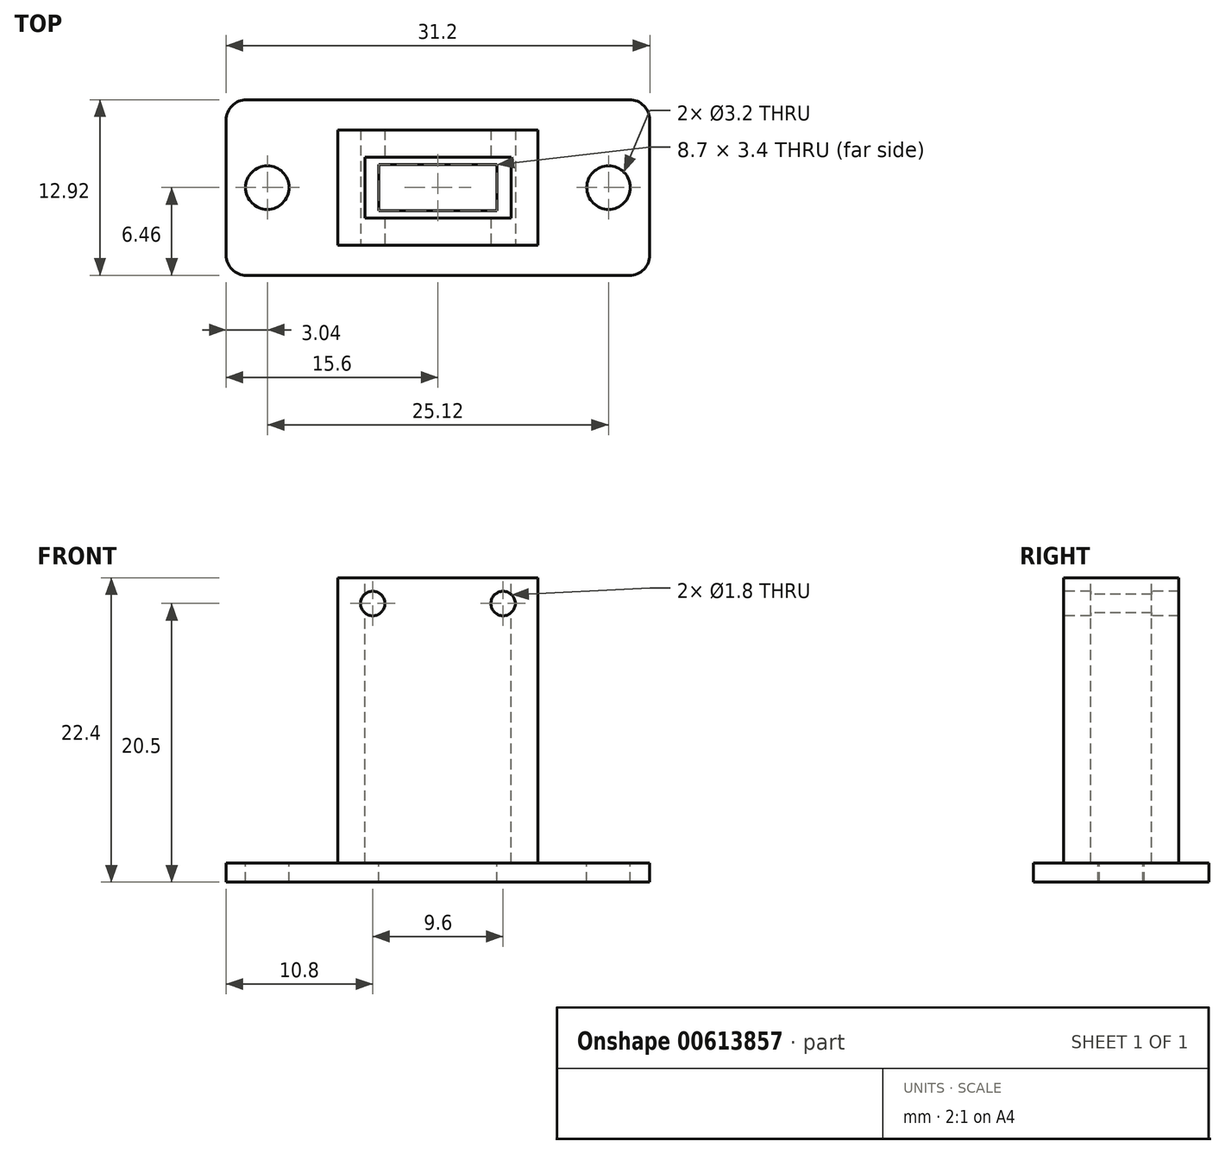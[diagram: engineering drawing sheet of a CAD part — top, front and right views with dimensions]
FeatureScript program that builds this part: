
annotation { "Feature Type Name" : "Feature", "Feature Type Description" : "" }
export const myFeature = defineFeature(function(context is Context, id is Id, definition is map)
    precondition{}
    {
        {
            var Q0;
            Q0=qCreatedBy(makeId("Top.planeOp"),FACE);
            var sketch = newSketch(context, id + "F0", { "sketchPlane" : qUnion([Q0])});
            skLineSegment(sketch, "E0.bottom", {"start": v(-15.6, 6.46) * mm, "end": v(15.6, 6.46) * mm});
            skLineSegment(sketch, "E0.top", {"start": v(-15.6, -6.46) * mm, "end": v(15.6, -6.46) * mm});
            skLineSegment(sketch, "E0.left", {"start": v(-15.6, 6.46) * mm, "end": v(-15.6, -6.46) * mm});
            skLineSegment(sketch, "E0.right", {"start": v(15.6, 6.46) * mm, "end": v(15.6, -6.46) * mm});
            skPoint(sketch, "E1", {"position": v(-15.6, 0) * mm});
            skPoint(sketch, "E2", {"position": v(0, 6.46) * mm});
            skSolve(sketch);
        }
        {
            var Q0;
            Q0 = qSketchRegion(id + "F0", true);
            extrude(context, id + "F1", {"entities" : qUnion([Q0]), "depth" : 1.4 * mm, "offsetDistance" : 25 * mm});
        }
        {
            var Q0;
            Q0=makeQuery(id+"F1.opExtrude","CAP_FACE",FACE,{"disambiguationData":[OSD([sQuery(id+"F0.wireOp",EDGE,"E0.bottom"),sQuery(id+"F0.wireOp",EDGE,"E0.top"),sQuery(id+"F0.wireOp",EDGE,"E0.left"),sQuery(id+"F0.wireOp",EDGE,"E0.right")])],"isStart":false});
            var sketch = newSketch(context, id + "F2", { "sketchPlane" : qUnion([Q0])});
            skCircle(sketch, "E3", {"center": v(-12.56, 0) * mm, "radius": 1.6 * mm});
            skCircle(sketch, "E4", {"center": v(12.56, 0) * mm, "radius": 1.6 * mm});
            skSolve(sketch);
        }
        {
            var Q0;
            Q0 = qSketchRegion(id + "F2", true);
            extrude(context, id + "F3", {"entities" : qUnion([Q0]), "operationType" : NewBodyOperationType.REMOVE, "endBound" : BoundingType.THROUGH_ALL, "oppositeDirection" : true, "depth" : 25 * mm, "offsetDistance" : 25 * mm});
        }
        {
            var Q0;
            Q0=makeQuery(id+"F1.opExtrude","SWEPT_EDGE",EDGE,{"disambiguationData":[OSD([sQuery(id+"F0.wireOp",EDGE,"E0.top"),sQuery(id+"F0.wireOp",EDGE,"E0.right")])]});
            var Q1;
            Q1=makeQuery(id+"F1.opExtrude","SWEPT_EDGE",EDGE,{"disambiguationData":[OSD([sQuery(id+"F0.wireOp",EDGE,"E0.bottom"),sQuery(id+"F0.wireOp",EDGE,"E0.right")])]});
            var Q2;
            Q2=makeQuery(id+"F1.opExtrude","SWEPT_EDGE",EDGE,{"disambiguationData":[OSD([sQuery(id+"F0.wireOp",EDGE,"E0.top"),sQuery(id+"F0.wireOp",EDGE,"E0.left")])]});
            var Q3;
            Q3=makeQuery(id+"F1.opExtrude","SWEPT_EDGE",EDGE,{"disambiguationData":[OSD([sQuery(id+"F0.wireOp",EDGE,"E0.bottom"),sQuery(id+"F0.wireOp",EDGE,"E0.left")])]});
            fillet(context, id + "F4", {"entities" : qUnion([Q0, Q1, Q2, Q3]), "radius" : 1.5 * mm, "tangentPropagation" : true, "allowEdgeOverflow" : false});
        }
        {
            var Q0;
            Q0=makeQuery(id+"F1.opExtrude","CAP_FACE",FACE,{"disambiguationData":[OSD([sQuery(id+"F0.wireOp",EDGE,"E0.bottom"),sQuery(id+"F0.wireOp",EDGE,"E0.top"),sQuery(id+"F0.wireOp",EDGE,"E0.left"),sQuery(id+"F0.wireOp",EDGE,"E0.right")])],"isStart":false});
            var sketch = newSketch(context, id + "F5", { "sketchPlane" : qUnion([Q0])});
            skLineSegment(sketch, "E5.bottom", {"start": v(-4.35, 1.7) * mm, "end": v(4.35, 1.7) * mm});
            skLineSegment(sketch, "E5.top", {"start": v(-4.35, -1.7) * mm, "end": v(4.35, -1.7) * mm});
            skLineSegment(sketch, "E5.left", {"start": v(-4.35, 1.7) * mm, "end": v(-4.35, -1.7) * mm});
            skLineSegment(sketch, "E5.right", {"start": v(4.35, 1.7) * mm, "end": v(4.35, -1.7) * mm});
            skPoint(sketch, "E6", {"position": v(-4.35, 0) * mm});
            skPoint(sketch, "E7", {"position": v(0, -1.7) * mm});
            skSolve(sketch);
        }
        {
            var Q0;
            Q0 = qSketchRegion(id + "F5", true);
            extrude(context, id + "F6", {"entities" : qUnion([Q0]), "operationType" : NewBodyOperationType.REMOVE, "endBound" : BoundingType.THROUGH_ALL, "oppositeDirection" : true, "depth" : 25 * mm, "offsetDistance" : 25 * mm});
        }
        {
            var Q0;
            Q0=makeQuery(id+"F1.opExtrude","CAP_FACE",FACE,{"disambiguationData":[OSD([sQuery(id+"F0.wireOp",EDGE,"E0.bottom"),sQuery(id+"F0.wireOp",EDGE,"E0.top"),sQuery(id+"F0.wireOp",EDGE,"E0.left"),sQuery(id+"F0.wireOp",EDGE,"E0.right")])],"isStart":false});
            var sketch = newSketch(context, id + "F7", { "sketchPlane" : qUnion([Q0])});
            skLineSegment(sketch, "E8.bottom", {"start": v(-7.38, 4.25) * mm, "end": v(7.38, 4.25) * mm});
            skLineSegment(sketch, "E8.top", {"start": v(-7.38, -4.25) * mm, "end": v(7.38, -4.25) * mm});
            skLineSegment(sketch, "E8.left", {"start": v(-7.38, 4.25) * mm, "end": v(-7.38, -4.25) * mm});
            skLineSegment(sketch, "E8.right", {"start": v(7.38, 4.25) * mm, "end": v(7.38, -4.25) * mm});
            skPoint(sketch, "E9", {"position": v(-7.38, 0) * mm});
            skPoint(sketch, "E10", {"position": v(0, -4.25) * mm});
            skSolve(sketch);
        }
        {
            var Q0;
            Q0 = qSketchRegion(id + "F7", true);
            extrude(context, id + "F8", {"entities" : qUnion([Q0]), "operationType" : NewBodyOperationType.ADD, "depth" : 21 * mm, "offsetDistance" : 25 * mm});
        }
        {
            var Q0;
            Q0=makeQuery(id+"F8.opExtrude","CAP_FACE",FACE,{"disambiguationData":[OSD([sQuery(id+"F7.wireOp",EDGE,"E8.bottom"),sQuery(id+"F7.wireOp",EDGE,"E8.top"),sQuery(id+"F7.wireOp",EDGE,"E8.left"),sQuery(id+"F7.wireOp",EDGE,"E8.right")])],"isStart":false});
            var sketch = newSketch(context, id + "F9", { "sketchPlane" : qUnion([Q0])});
            skLineSegment(sketch, "E11.bottom", {"start": v(-5.38, 2.25) * mm, "end": v(5.38, 2.25) * mm});
            skLineSegment(sketch, "E11.top", {"start": v(-5.38, -2.25) * mm, "end": v(5.38, -2.25) * mm});
            skLineSegment(sketch, "E11.left", {"start": v(-5.38, 2.25) * mm, "end": v(-5.38, -2.25) * mm});
            skLineSegment(sketch, "E11.right", {"start": v(5.38, 2.25) * mm, "end": v(5.38, -2.25) * mm});
            skPoint(sketch, "E12", {"position": v(0, 2.25) * mm});
            skPoint(sketch, "E13", {"position": v(5.38, 0) * mm});
            skSolve(sketch);
        }
        {
            var Q0;
            Q0 = qSketchRegion(id + "F9", true);
            var Q1;
            Q1=makeQuery(id+"F1.opExtrude","CAP_FACE",FACE,{"disambiguationData":[OSD([sQuery(id+"F0.wireOp",EDGE,"E0.bottom"),sQuery(id+"F0.wireOp",EDGE,"E0.top"),sQuery(id+"F0.wireOp",EDGE,"E0.left"),sQuery(id+"F0.wireOp",EDGE,"E0.right")])],"isStart":false});
            extrude(context, id + "F10", {"entities" : qUnion([Q0]), "operationType" : NewBodyOperationType.REMOVE, "endBound" : BoundingType.UP_TO_SURFACE, "oppositeDirection" : true, "depth" : 25 * mm, "endBoundEntityFace" : qUnion([Q1]), "offsetDistance" : 25 * mm});
        }
        {
            var Q0;
            Q0=makeQuery(id+"F8.opExtrude","SWEPT_FACE",FACE,{"disambiguationData":[OSD([sQuery(id+"F7.wireOp",EDGE,"E8.top")])]});
            var sketch = newSketch(context, id + "F11", { "sketchPlane" : qUnion([Q0])});
            skCircle(sketch, "E14", {"center": v(-4.8, 20.5) * mm, "radius": 0.9 * mm});
            skCircle(sketch, "E15.MirrorC", {"center": v(4.8, 20.5) * mm, "radius": 0.9 * mm});
            skSolve(sketch);
        }
        {
            var Q0;
            Q0 = qSketchRegion(id + "F11", true);
            extrude(context, id + "F12", {"entities" : qUnion([Q0]), "operationType" : NewBodyOperationType.REMOVE, "endBound" : BoundingType.THROUGH_ALL, "oppositeDirection" : true, "depth" : 25 * mm, "offsetDistance" : 25 * mm});
        }
    });
